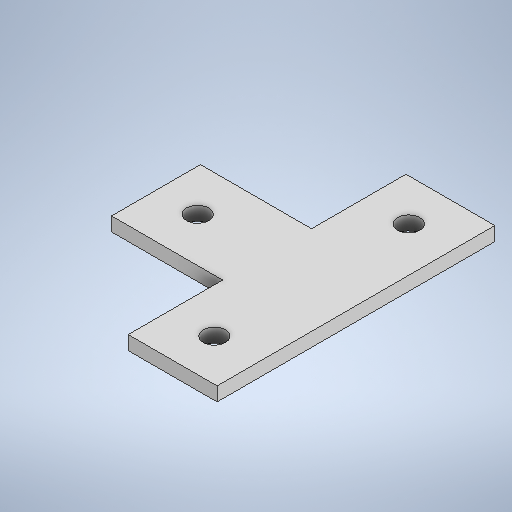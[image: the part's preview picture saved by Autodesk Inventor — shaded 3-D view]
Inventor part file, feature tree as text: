
AUTODESK INVENTOR PART (.ipt)
format: ipt  version: 2025.1 (Build 291241000, 241)  size: 235,520 bytes
history: native  units: in
note: dims shown in document units (in); Inventor stores cm internally (conversion verified against a paired STEP export)
features: extrude x1, sketch x1
ambient origin geometry x8: Origin, YZ Plane, XZ Plane, XY Plane, X Axis, Y Axis, Z Axis, Center Point
bodies: Solid1 (feature_tree)
feature tree (2):
  extrude  "Extrusion1"  Depth=2.5in
  sketch  "Sketch1"  dims[d0=0.8in d1=2.5in d2=1.0in d3=0.4in d4=0.4in d5=0.375in d6=0.375in d7=0.2in d8=0.2in d9=0.375in d10=0.2in d11=0.125in d12=0.0in]
